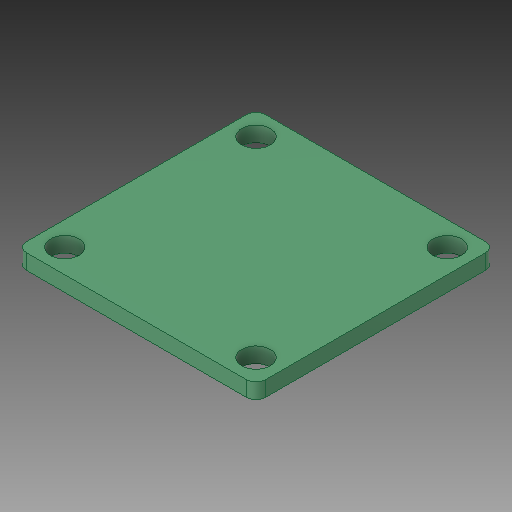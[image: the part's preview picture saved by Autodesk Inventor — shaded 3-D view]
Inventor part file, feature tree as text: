
AUTODESK INVENTOR PART (.ipt)
format: ipt  version: 2018.2 (Build 222227000, 227)  size: 115,200 bytes
history: native  units: mm
features: sketch x1, extrude x1, hole x1, fillet x1
ambient origin geometry x8: Origin, YZ Plane, XZ Plane, XY Plane, X Axis, Y Axis, Z Axis, Center Point
bodies: Solid1 (feature_tree)
feature tree (4):
  sketch  "Sketch1"  dims[d0=25.0mm d1=25.0mm d2=20.0mm d3=20.0mm d4=2.5mm d5=2.5mm d6=1.6mm d7=0.0mm d8=3.0mm d9=6.0mm d10=4.0mm d11=2.0mm d12=90.0deg d13=8.0mm d14=20.594885mm d15=1.0mm]
  extrude  "Extrusion1"  Depth=25.0mm
  hole  "Hole1"  [1 undecoded]
  fillet  "Fillet1"  Radius=20.0mm
note: 1 required parameter value undecoded (feature->parameter linkage not recoverable at this tier; creation-order binding heuristic only, values carry confidence <= 0.55)
